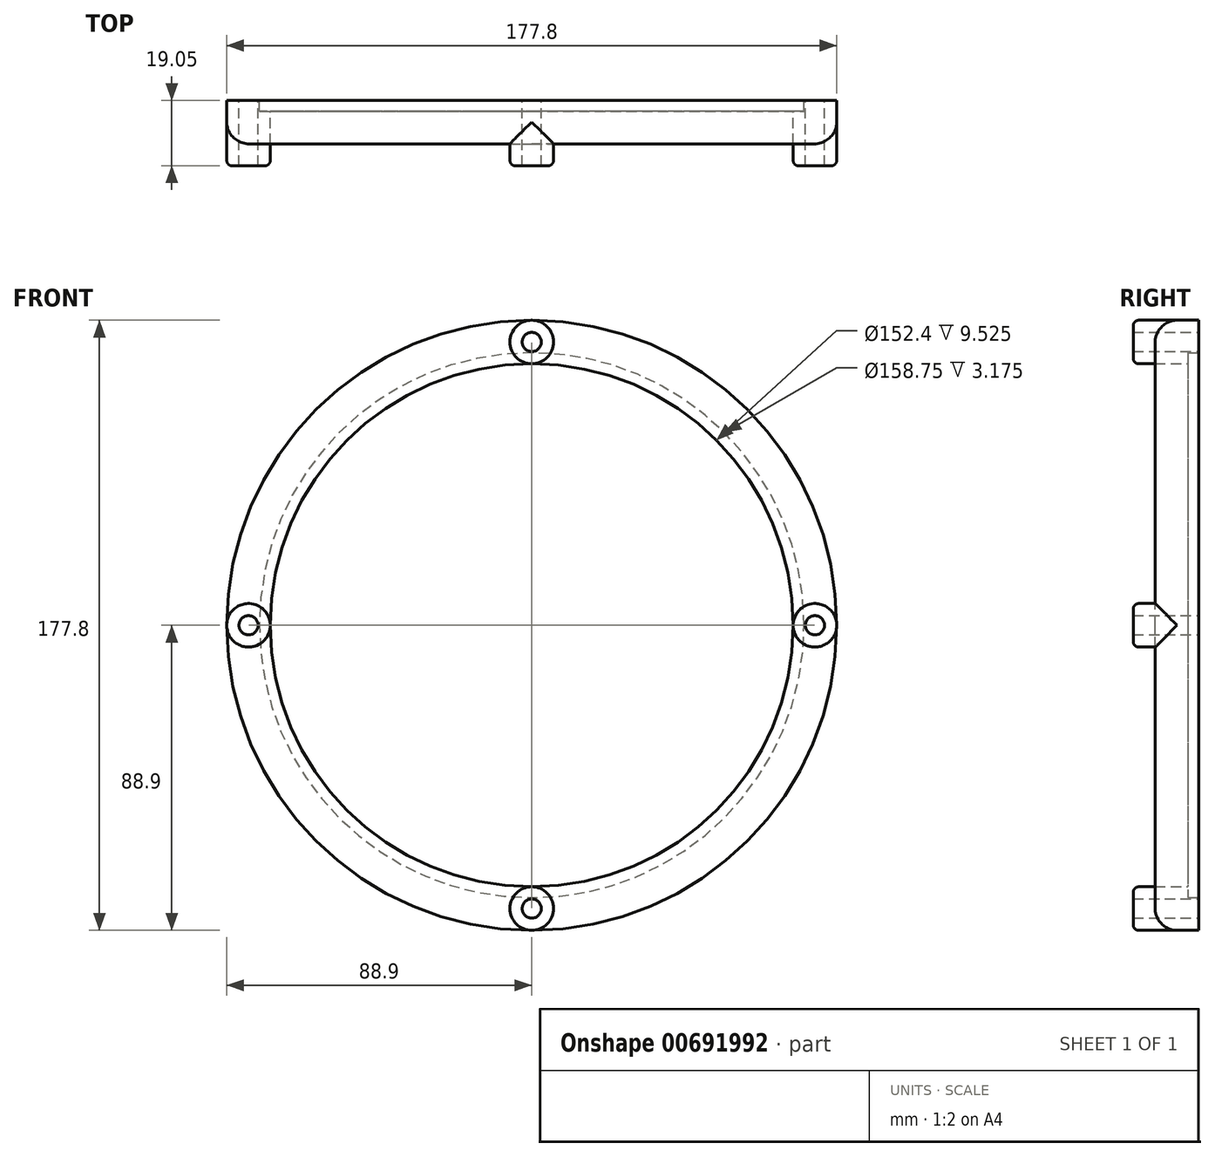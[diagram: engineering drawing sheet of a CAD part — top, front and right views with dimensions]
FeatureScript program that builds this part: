
annotation { "Feature Type Name" : "Feature", "Feature Type Description" : "" }
export const myFeature = defineFeature(function(context is Context, id is Id, definition is map)
    precondition{}
    {
        {
            var Q0;
            Q0=qCreatedBy(makeId("Front.planeOp"),FACE);
            var sketch = newSketch(context, id + "F0", { "sketchPlane" : qUnion([Q0])});
            skCircle(sketch, "E0", {"center": v(0, 0) * mm, "radius": 76.2 * mm});
            skPoint(sketch, "E1.center.orphan", {"position": v(1.5, 0) * mm});
            skCircle(sketch, "E2", {"center": v(0, 0) * mm, "radius": 88.9 * mm});
            skCircle(sketch, "E3", {"center": v(0, 0) * mm, "radius": 79.38 * mm});
            skSolve(sketch);
        }
        {
            var Q0;
            Q0 = qSketchRegion(id + "F0", true);
            var Q1;
            Q1=makeQuery(id+"F0.imprint","IMPRINT",FACE,{"disambiguationData":[TD([[makeQuery(id+"F0.imprint","IMPRINT",EDGE,{"derivedFrom":sQuery(id+"F0.wireOp",EDGE,"E0")}),-1.0]])]});
            extrude(context, id + "F1", {"entities" : qUnion([Q0, Q1]), "depth" : 12.7 * mm, "offsetDistance" : 30.48 * mm});
        }
        {
            var Q0;
            Q0=makeQuery(id+"F1.opExtrude","CAP_FACE",FACE,{"disambiguationData":[OSD([sQuery(id+"F0.wireOp",EDGE,"E1"),sQuery(id+"F0.wireOp",EDGE,"E0")])],"isStart":true});
            var sketch = newSketch(context, id + "F2", { "sketchPlane" : qUnion([Q0])});
            skCircle(sketch, "E4", {"center": v(0, 0) * mm, "radius": 79.38 * mm});
            skSolve(sketch);
        }
        {
            var Q0;
            Q0=makeQuery(id+"F0.imprint","IMPRINT",FACE,{"disambiguationData":[TD([[makeQuery(id+"F0.imprint","IMPRINT",EDGE,{"derivedFrom":sQuery(id+"F0.wireOp",EDGE,"E0")}),-1.0]])]});
            var sketch = newSketch(context, id + "F3", { "sketchPlane" : qUnion([Q0])});
            skLineSegment(sketch, "E5", {"start": v(0, 0) * mm, "end": v(0, 82.55) * mm});
            skLineSegment(sketch, "E6", {"start": v(0, 0) * mm, "end": v(82.55, 0) * mm});
            skLineSegment(sketch, "E7", {"start": v(0, 0) * mm, "end": v(-82.55, 0) * mm});
            skLineSegment(sketch, "E8", {"start": v(0, 0) * mm, "end": v(0, -82.55) * mm});
            skCircle(sketch, "E9", {"center": v(0, 82.55) * mm, "radius": 6.35 * mm});
            skCircle(sketch, "E10", {"center": v(82.55, 0) * mm, "radius": 6.35 * mm});
            skCircle(sketch, "E11", {"center": v(0, -82.55) * mm, "radius": 6.35 * mm});
            skCircle(sketch, "E12", {"center": v(-82.55, 0) * mm, "radius": 6.35 * mm});
            skSolve(sketch);
        }
        {
            var Q0;
            Q0 = qSketchRegion(id + "F3", true);
            extrude(context, id + "F4", {"entities" : qUnion([Q0]), "operationType" : NewBodyOperationType.ADD, "depth" : 19.05 * mm, "offsetDistance" : 25.4 * mm});
        }
        {
            var Q0;
            Q0=qCreatedBy(makeId("Front.planeOp"),FACE);
            var sketch = newSketch(context, id + "F5", { "sketchPlane" : qUnion([Q0])});
            skLineSegment(sketch, "E13", {"start": v(0, 0) * mm, "end": v(0, 82.55) * mm});
            skLineSegment(sketch, "E14", {"start": v(0, 0) * mm, "end": v(0, -82.55) * mm});
            skLineSegment(sketch, "E15", {"start": v(0, 0) * mm, "end": v(-82.55, 0) * mm});
            skLineSegment(sketch, "E16", {"start": v(0, 0) * mm, "end": v(82.55, 0) * mm});
            skCircle(sketch, "E17", {"center": v(82.55, 0) * mm, "radius": 2.8 * mm});
            skCircle(sketch, "E18", {"center": v(0, 82.55) * mm, "radius": 2.8 * mm});
            skCircle(sketch, "E19", {"center": v(-82.55, 0) * mm, "radius": 2.8 * mm});
            skCircle(sketch, "E20", {"center": v(0, -82.55) * mm, "radius": 2.8 * mm});
            skSolve(sketch);
        }
        {
            var Q0;
            Q0 = qSketchRegion(id + "F5", true);
            extrude(context, id + "F6", {"entities" : qUnion([Q0]), "operationType" : NewBodyOperationType.REMOVE, "endBound" : BoundingType.THROUGH_ALL, "depth" : 25.4 * mm, "offsetDistance" : 25.4 * mm});
        }
        {
            var Q0;
            Q0=makeQuery(id+"F1.opExtrude","CAP_EDGE",EDGE,{"disambiguationData":[OSD([sQuery(id+"F0.wireOp",EDGE,"E2")])],"isStart":false});
            fillet(context, id + "F7", {"entities" : qUnion([Q0]), "tangentPropagation" : true, "radius" : 6.35 * mm, "defaultsChanged" : true, "vertexSettings" : [], "allowEdgeOverflow" : false});
        }
        {
            var Q0;
            Q0 = qSketchRegion(id + "F2", true);
            extrude(context, id + "F8", {"entities" : qUnion([Q0]), "operationType" : NewBodyOperationType.REMOVE, "oppositeDirection" : true, "depth" : 3.17 * mm, "offsetDistance" : 25.4 * mm});
        }
        {
            var Q0;
            Q0=makeQuery(id+"F4.opExtrude","CAP_EDGE",EDGE,{"disambiguationData":[OSD([sQuery(id+"F3.wireOp",EDGE,"E9")])],"isStart":false});
            var Q1;
            Q1=makeQuery(id+"F4.opExtrude","CAP_EDGE",EDGE,{"disambiguationData":[OSD([sQuery(id+"F3.wireOp",EDGE,"E10")])],"isStart":false});
            var Q2;
            Q2=makeQuery(id+"F4.opExtrude","CAP_EDGE",EDGE,{"disambiguationData":[OSD([sQuery(id+"F3.wireOp",EDGE,"E11")])],"isStart":false});
            var Q3;
            Q3=makeQuery(id+"F4.opExtrude","CAP_EDGE",EDGE,{"disambiguationData":[OSD([sQuery(id+"F3.wireOp",EDGE,"E12")])],"isStart":false});
            fillet(context, id + "F9", {"entities" : qUnion([Q0, Q1, Q2, Q3]), "tangentPropagation" : true, "radius" : 1.59 * mm, "defaultsChanged" : true, "vertexSettings" : [], "allowEdgeOverflow" : false});
        }
    });
